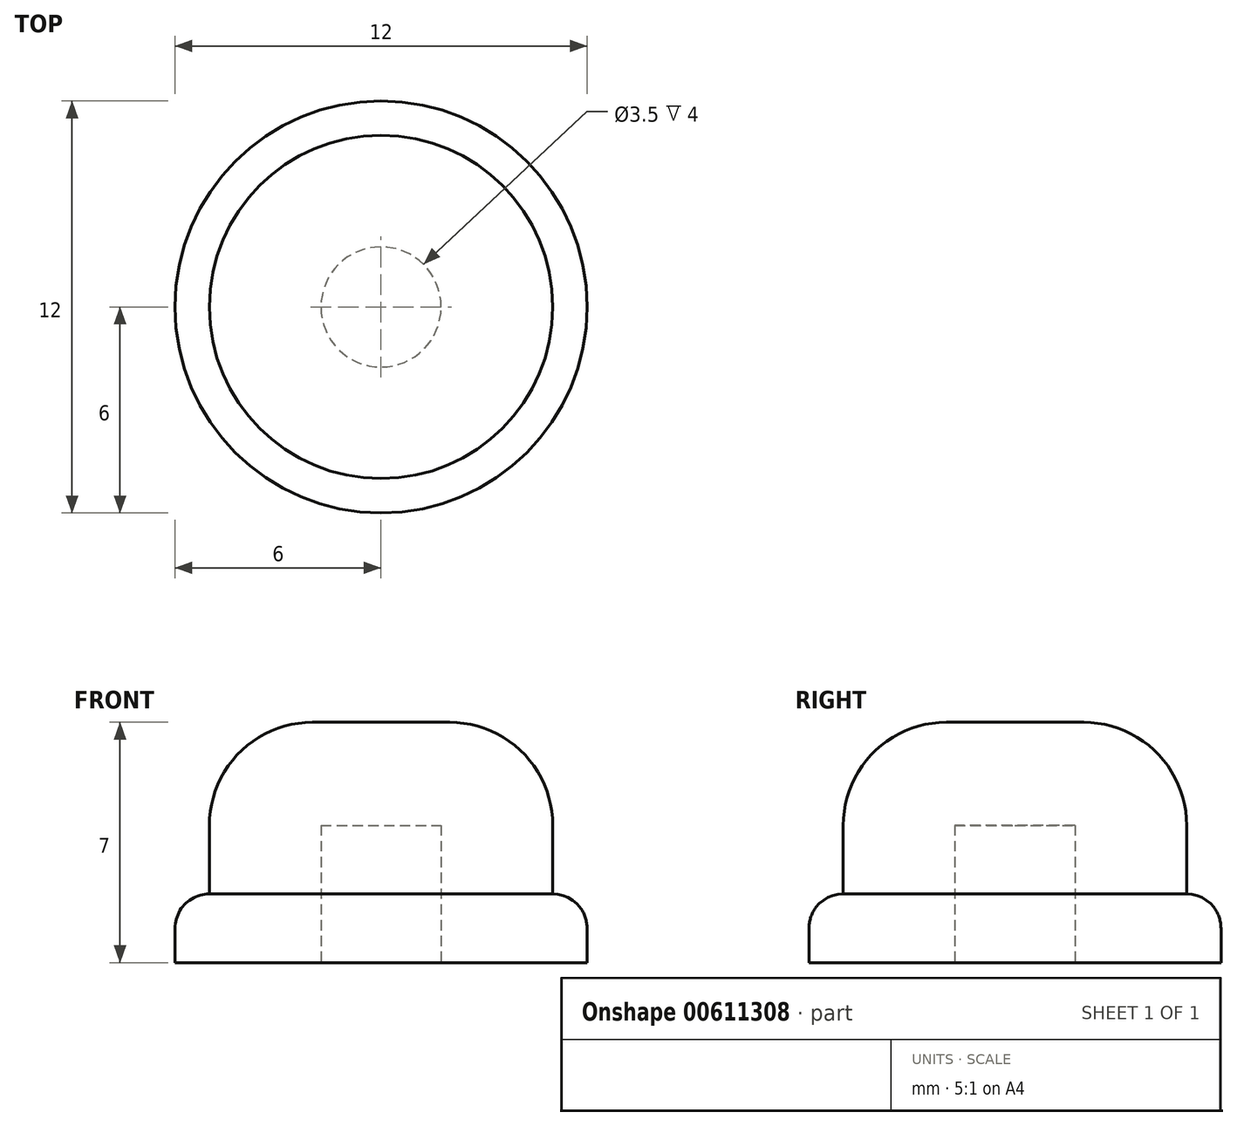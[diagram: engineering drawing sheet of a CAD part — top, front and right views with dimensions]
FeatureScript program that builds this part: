
annotation { "Feature Type Name" : "Feature", "Feature Type Description" : "" }
export const myFeature = defineFeature(function(context is Context, id is Id, definition is map)
    precondition{}
    {
        {
            var Q0;
            Q0=qCreatedBy(makeId("Top.planeOp"),FACE);
            var sketch = newSketch(context, id + "F0", { "sketchPlane" : qUnion([Q0])});
            skCircle(sketch, "E0", {"center": v(0, 0) * mm, "radius": 5 * mm});
            skSolve(sketch);
        }
        {
            var Q0;
            Q0=makeQuery(id+"F0.imprint","IMPRINT",FACE,{"disambiguationData":[TD([[makeQuery(id+"F0.imprint","IMPRINT",EDGE,{"derivedFrom":sQuery(id+"F0.wireOp",EDGE,"E0")}),1.0]])]});
            extrude(context, id + "F1", {"entities" : qUnion([Q0]), "depth" : 5 * mm, "offsetDistance" : 25 * mm});
        }
        {
            var Q0;
            Q0=makeQuery(id+"F1.opExtrude","CAP_EDGE",EDGE,{"disambiguationData":[OSD([sQuery(id+"F0.wireOp",EDGE,"E0")])],"isStart":false});
            fillet(context, id + "F2", {"entities" : qUnion([Q0]), "radius" : 3 * mm, "tangentPropagation" : true, "allowEdgeOverflow" : false});
        }
        {
            var Q0;
            Q0=makeQuery(id+"F1.opExtrude","CAP_FACE",FACE,{"disambiguationData":[OSD([sQuery(id+"F0.wireOp",EDGE,"E0")])],"isStart":true});
            var sketch = newSketch(context, id + "F3", { "sketchPlane" : qUnion([Q0])});
            skCircle(sketch, "E1", {"center": v(0, 0) * mm, "radius": 6 * mm});
            skSolve(sketch);
        }
        {
            var Q0;
            Q0=makeQuery(id+"F3.imprint","IMPRINT",FACE,{"disambiguationData":[TD([[makeQuery(id+"F3.imprint","IMPRINT",EDGE,{"derivedFrom":sQuery(id+"F3.wireOp",EDGE,"E1")}),1.0]])]});
            var Q1;
            Q1=makeQuery(id+"F3.imprint","IMPRINT",FACE,{"disambiguationData":[TD([[makeQuery(id+"F3.imprint","IMPRINT",EDGE,{"derivedFrom":makeQuery(id+"F1.opExtrude","CAP_EDGE",EDGE,{"disambiguationData":[OSD([sQuery(id+"F0.wireOp",EDGE,"E0")])],"isStart":true})}),-1.0]])]});
            extrude(context, id + "F4", {"entities" : qUnion([Q0, Q1]), "operationType" : NewBodyOperationType.ADD, "depth" : 2 * mm, "offsetDistance" : 25 * mm});
        }
        {
            var Q0;
            Q0=makeQuery(id+"F4.opExtrude","CAP_EDGE",EDGE,{"disambiguationData":[OSD([sQuery(id+"F3.wireOp",EDGE,"E1")])],"isStart":true});
            fillet(context, id + "F5", {"entities" : qUnion([Q0]), "radius" : 1 * mm, "tangentPropagation" : true, "allowEdgeOverflow" : false});
        }
        {
            var Q0;
            Q0=makeQuery(id+"F4.opExtrude","CAP_FACE",FACE,{"disambiguationData":[OSD([sQuery(id+"F3.wireOp",EDGE,"E1")])],"isStart":false});
            var sketch = newSketch(context, id + "F6", { "sketchPlane" : qUnion([Q0])});
            skCircle(sketch, "E2", {"center": v(0, 0) * mm, "radius": 1.75 * mm});
            skSolve(sketch);
        }
        {
            var Q0;
            Q0=makeQuery(id+"F6.imprint","IMPRINT",FACE,{"disambiguationData":[TD([[makeQuery(id+"F6.imprint","IMPRINT",EDGE,{"derivedFrom":sQuery(id+"F6.wireOp",EDGE,"E2")}),1.0]])]});
            var Q1;
            Q1=sQuery(id+"F6.wireOp",EDGE,"E2");
            extrude(context, id + "F7", {"entities" : qUnion([Q0]), "operationType" : NewBodyOperationType.REMOVE, "surfaceEntities" : qUnion([Q1]), "oppositeDirection" : true, "depth" : 4 * mm, "offsetDistance" : 25 * mm});
        }
    });
